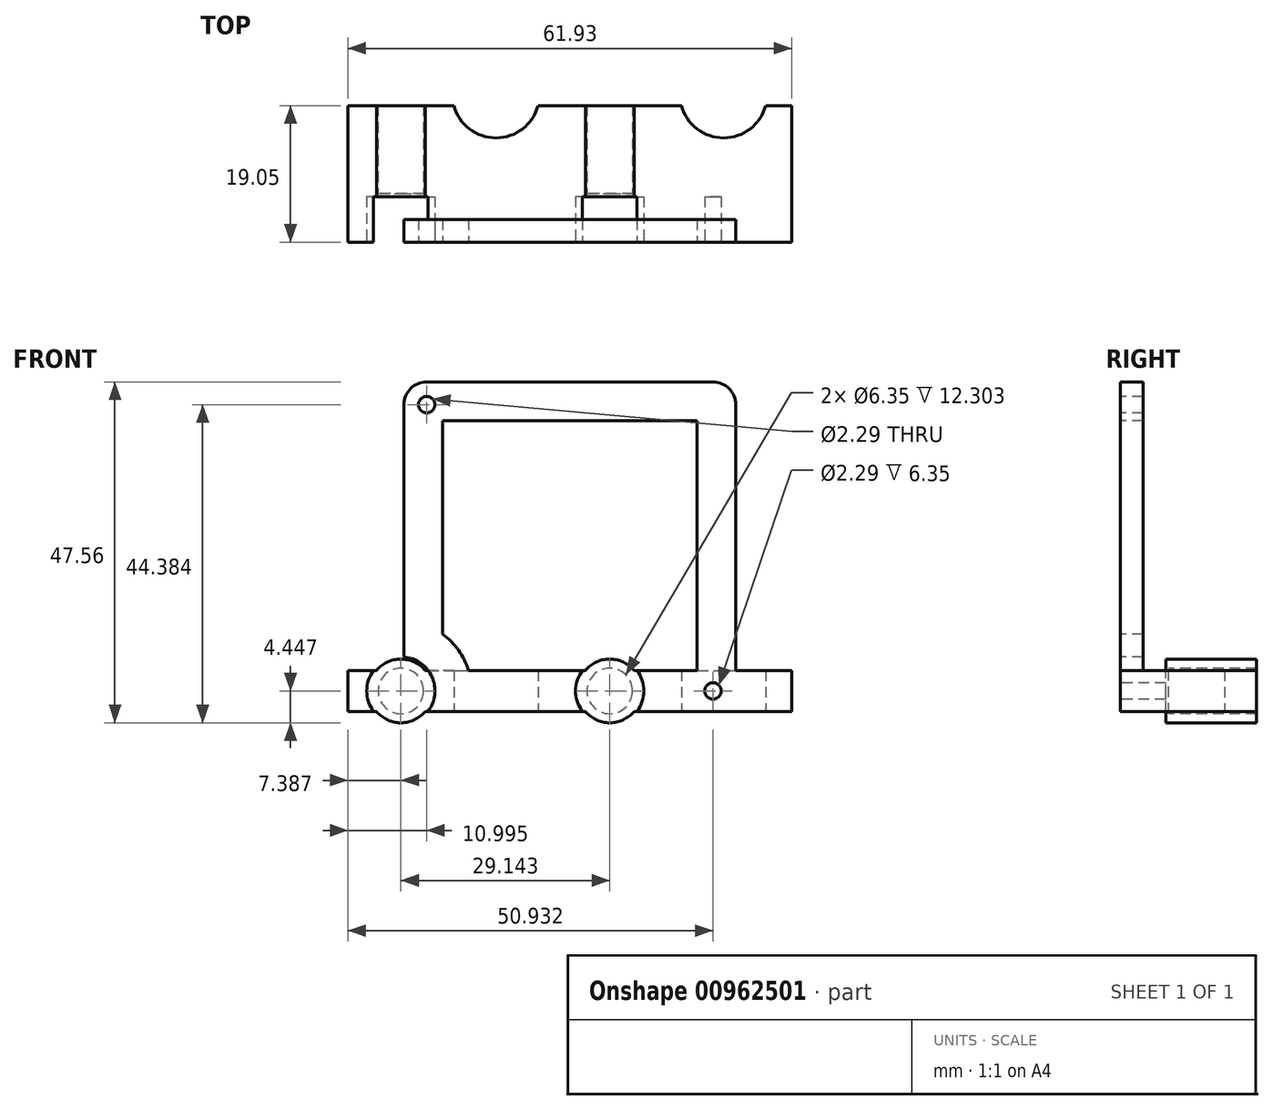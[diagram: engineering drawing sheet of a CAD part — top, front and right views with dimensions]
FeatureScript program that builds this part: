
annotation { "Feature Type Name" : "Feature", "Feature Type Description" : "" }
export const myFeature = defineFeature(function(context is Context, id is Id, definition is map)
    precondition{}
    {
        {
            var Q0;
            Q0=qCreatedBy(makeId("Top.planeOp"),FACE);
            var sketch = newSketch(context, id + "F0", { "sketchPlane" : qUnion([Q0])});
            skArc(sketch, "E0", {"start": v(-21.76, -1.59) * mm, "mid": v(-15.88, -6.1) * mm, "end": v(-9.99, -1.59) * mm});
            skArc(sketch, "E1", {"start": v(9.99, -1.59) * mm, "mid": v(15.88, -6.1) * mm, "end": v(21.76, -1.59) * mm});
            skLineSegment(sketch, "E2", {"start": v(-21.76, -1.59) * mm, "end": v(-36.53, -1.59) * mm});
            skLineSegment(sketch, "E3", {"start": v(-36.53, -1.59) * mm, "end": v(-36.53, -20.64) * mm});
            skLineSegment(sketch, "E4", {"start": v(-36.53, -20.64) * mm, "end": v(25.4, -20.64) * mm});
            skLineSegment(sketch, "E5", {"start": v(25.4, -20.64) * mm, "end": v(25.4, -1.59) * mm});
            skLineSegment(sketch, "E6", {"start": v(25.4, -1.59) * mm, "end": v(21.76, -1.59) * mm});
            skLineSegment(sketch, "E7", {"start": v(9.99, -1.59) * mm, "end": v(-9.99, -1.59) * mm});
            skSolve(sketch);
        }
        {
            var Q0;
            Q0 = qSketchRegion(id + "F0", true);
            extrude(context, id + "F1", {"entities" : qUnion([Q0]), "depth" : 5.7 * mm, "offsetDistance" : 25.4 * mm});
        }
        {
            var Q0;
            Q0=makeQuery(id+"F1.opExtrude","SWEPT_FACE",FACE,{"disambiguationData":[OSD([sQuery(id+"F0.wireOp",EDGE,"E4")])]});
            var sketch = newSketch(context, id + "F2", { "sketchPlane" : qUnion([Q0])});
            skCircle(sketch, "E8", {"center": v(-5.56, 2.86) * mm, "radius": 2.86 * mm, "construction": true});
            skCircle(sketch, "E9", {"center": v(-25.53, 42.8) * mm, "radius": 1.14 * mm});
            skLineSegment(sketch, "E10", {"start": v(-28.7, 42.8) * mm, "end": v(-28.7, 5.71) * mm});
            skLineSegment(sketch, "E11", {"start": v(-28.7, 5.71) * mm, "end": v(-23.29, 5.72) * mm});
            skLineSegment(sketch, "E12", {"start": v(-23.29, 5.72) * mm, "end": v(-23.29, 40.55) * mm});
            skPoint(sketch, "E13.top.start.orphan", {"position": v(-29.18, -20.76) * mm});
            skCircle(sketch, "E14", {"center": v(14.4, 2.86) * mm, "radius": 1.14 * mm});
            skLineSegment(sketch, "E15", {"start": v(-25.53, 42.8) * mm, "end": v(14.4, 2.86) * mm, "construction": true});
            skArc(sketch, "E16", {"start": v(17.58, 42.8) * mm, "mid": v(16.65, 45.04) * mm, "end": v(14.4, 45.97) * mm});
            skLineSegment(sketch, "E17", {"start": v(17.58, 42.8) * mm, "end": v(17.58, 5.72) * mm});
            skLineSegment(sketch, "E18", {"start": v(12.16, 5.72) * mm, "end": v(17.58, 5.71) * mm});
            skLineSegment(sketch, "E19", {"start": v(-25.53, 45.97) * mm, "end": v(14.4, 45.97) * mm});
            skArc(sketch, "E20", {"start": v(-25.53, 45.97) * mm, "mid": v(-27.78, 45.04) * mm, "end": v(-28.7, 42.8) * mm});
            skLineSegment(sketch, "E21", {"start": v(-23.29, 40.55) * mm, "end": v(12.16, 40.55) * mm});
            skLineSegment(sketch, "E22", {"start": v(12.16, 40.55) * mm, "end": v(12.16, 5.72) * mm});
            skSolve(sketch);
        }
        {
            var Q0;
            Q0 = qSketchRegion(id + "F2", true);
            extrude(context, id + "F3", {"entities" : qUnion([Q0]), "operationType" : NewBodyOperationType.ADD, "oppositeDirection" : true, "depth" : 3.17 * mm, "offsetDistance" : 25.4 * mm});
        }
        {
            var Q0;
            Q0=makeQuery(id+"F3.boolean.opBoolean","MERGE",FACE,{"derivedFrom":[makeQuery(id+"F1.opExtrude","SWEPT_FACE",FACE,{"disambiguationData":[OSD([sQuery(id+"F0.wireOp",EDGE,"E4")])]}),makeQuery(id+"F3.opExtrude","CAP_FACE",FACE,{"disambiguationData":[OSD([sQuery(id+"F2.wireOp",EDGE,"E9"),sQuery(id+"F2.wireOp",EDGE,"GDH4g0oQ-nd7Q-Zn2g-Z2z6-5aHBvg0Lr09C"),sQuery(id+"F2.wireOp",EDGE,"E10"),sQuery(id+"F2.wireOp",EDGE,"E11"),sQuery(id+"F2.wireOp",EDGE,"E12")])],"isStart":true}),makeQuery(id+"F3.opExtrude","CAP_FACE",FACE,{"disambiguationData":[OSD([sQuery(id+"F2.wireOp",EDGE,"nM6Eh8F1-qOBL-3qUv-6L2V-JEi5WRzBgLFH"),sQuery(id+"F2.wireOp",EDGE,"JC2lydbS-xeSN-gWn7-KMeQ-zuUTK9r0PLlo"),sQuery(id+"F2.wireOp",EDGE,"ONUtfR4M-aSmu-eGrm-hsvk-2R0VDrcKPRzi"),sQuery(id+"F2.wireOp",EDGE,"0aukuiJN-D17R-zCOD-Oj78-UeWdiGfD59D5"),sQuery(id+"F2.wireOp",EDGE,"T4R5p8lt-zdvz-CFuB-Jltc-x5WoAOuWlztu")])],"isStart":true})]});
            var sketch = newSketch(context, id + "F4", { "sketchPlane" : qUnion([Q0])});
            skCircle(sketch, "E23", {"center": v(-29.14, 2.86) * mm, "radius": 3.18 * mm});
            skCircle(sketch, "E24", {"center": v(0, 2.86) * mm, "radius": 3.18 * mm});
            skLineSegment(sketch, "E25", {"start": v(-36.53, 2.86) * mm, "end": v(-21.76, 2.86) * mm, "construction": true});
            skLineSegment(sketch, "E26", {"start": v(-9.99, 2.86) * mm, "end": v(9.99, 2.86) * mm, "construction": true});
            skSolve(sketch);
        }
        {
            var Q0;
            {var subQ0=sQuery(id+"F2.wireOp",EDGE,"E20");var subQ1=sQuery(id+"F2.wireOp",EDGE,"E19");var subQ2=sQuery(id+"F2.wireOp",EDGE,"E16");var subQ3=sQuery(id+"F2.wireOp",EDGE,"E10");var subQ4=sQuery(id+"F2.wireOp",EDGE,"E17");var subQ7=sQuery(id+"F0.wireOp",EDGE,"E5");var subQ8=sQuery(id+"F0.wireOp",EDGE,"E4");var subQ13=sQuery(id+"F2.wireOp",EDGE,"E9");var subQ14=sQuery(id+"F2.wireOp",EDGE,"E12");var subQ15=sQuery(id+"F2.wireOp",EDGE,"E21");var subQ16=sQuery(id+"F2.wireOp",EDGE,"E22");Q0=makeQuery(id+"F9.boolean.opBoolean","SPLIT",FACE,{"disambiguationData":[TD([makeQuery(id+"F1.opExtrude","SWEPT_FACE",FACE,{"disambiguationData":[OSD([subQ7])]})])],"derivedFrom":makeQuery(id+"F3.boolean.opBoolean","MERGE",FACE,{"derivedFrom":[makeQuery(id+"F1.opExtrude","SWEPT_FACE",FACE,{"disambiguationData":[OSD([subQ8])]}),makeQuery(id+"F3.opExtrude","CAP_FACE",FACE,{"disambiguationData":[OSD([subQ13,subQ3,sQuery(id+"F2.wireOp",EDGE,"E11"),subQ14,subQ2,subQ4,sQuery(id+"F2.wireOp",EDGE,"E18"),subQ1,subQ0,subQ15,subQ16])],"isStart":true})]})});}
            var sketch = newSketch(context, id + "F5", { "sketchPlane" : qUnion([Q0])});
            skCircle(sketch, "E27", {"center": v(-29.14, 2.86) * mm, "radius": 4.45 * mm});
            skCircle(sketch, "E28", {"center": v(0, 2.86) * mm, "radius": 4.45 * mm});
            skSolve(sketch);
        }
        {
            var Q0;
            Q0 = qSketchRegion(id + "F5", true);
            var Q1;
            Q1=makeQuery(id+"F1.opExtrude","SWEPT_FACE",FACE,{"disambiguationData":[OSD([sQuery(id+"F0.wireOp",EDGE,"E2")])]});
            extrude(context, id + "F6", {"entities" : qUnion([Q0]), "operationType" : NewBodyOperationType.ADD, "endBound" : BoundingType.UP_TO_SURFACE, "oppositeDirection" : true, "depth" : 25.4 * mm, "endBoundEntityFace" : qUnion([Q1]), "offsetDistance" : 25.4 * mm});
        }
        {
            var Q0;
            Q0 = qSketchRegion(id + "F4", true);
            extrude(context, id + "F7", {"entities" : qUnion([Q0]), "operationType" : NewBodyOperationType.REMOVE, "endBound" : BoundingType.UP_TO_NEXT, "oppositeDirection" : true, "depth" : 23.37 * mm, "offsetDistance" : 25.4 * mm});
        }
        {
            var Q0;
            Q0=makeQuery(id+"F3.boolean.opBoolean","MERGE",FACE,{"derivedFrom":[makeQuery(id+"F1.opExtrude","SWEPT_FACE",FACE,{"disambiguationData":[OSD([sQuery(id+"F0.wireOp",EDGE,"E4")])]}),makeQuery(id+"F3.opExtrude","CAP_FACE",FACE,{"disambiguationData":[OSD([sQuery(id+"F2.wireOp",EDGE,"E9"),sQuery(id+"F2.wireOp",EDGE,"GDH4g0oQ-nd7Q-Zn2g-Z2z6-5aHBvg0Lr09C"),sQuery(id+"F2.wireOp",EDGE,"E10"),sQuery(id+"F2.wireOp",EDGE,"E11"),sQuery(id+"F2.wireOp",EDGE,"E12")])],"isStart":true}),makeQuery(id+"F3.opExtrude","CAP_FACE",FACE,{"disambiguationData":[OSD([sQuery(id+"F2.wireOp",EDGE,"nM6Eh8F1-qOBL-3qUv-6L2V-JEi5WRzBgLFH"),sQuery(id+"F2.wireOp",EDGE,"JC2lydbS-xeSN-gWn7-KMeQ-zuUTK9r0PLlo"),sQuery(id+"F2.wireOp",EDGE,"ONUtfR4M-aSmu-eGrm-hsvk-2R0VDrcKPRzi"),sQuery(id+"F2.wireOp",EDGE,"0aukuiJN-D17R-zCOD-Oj78-UeWdiGfD59D5"),sQuery(id+"F2.wireOp",EDGE,"T4R5p8lt-zdvz-CFuB-Jltc-x5WoAOuWlztu")])],"isStart":true})]});
            var sketch = newSketch(context, id + "F8", { "sketchPlane" : qUnion([Q0])});
            skCircle(sketch, "E29", {"center": v(-29.14, 2.86) * mm, "radius": 4.76 * mm});
            skCircle(sketch, "E30", {"center": v(0, 2.86) * mm, "radius": 4.76 * mm});
            skSolve(sketch);
        }
        {
            var Q0;
            Q0 = qSketchRegion(id + "F8", true);
            extrude(context, id + "F9", {"entities" : qUnion([Q0]), "operationType" : NewBodyOperationType.REMOVE, "oppositeDirection" : true, "depth" : 6.35 * mm, "offsetDistance" : 25.4 * mm});
        }
        {
            var Q0;
            {var subQ0=sQuery(id+"F2.wireOp",EDGE,"E20");var subQ1=sQuery(id+"F2.wireOp",EDGE,"E19");var subQ2=sQuery(id+"F2.wireOp",EDGE,"E16");var subQ3=sQuery(id+"F2.wireOp",EDGE,"E10");var subQ4=sQuery(id+"F2.wireOp",EDGE,"E17");var subQ7=sQuery(id+"F0.wireOp",EDGE,"E5");var subQ8=sQuery(id+"F0.wireOp",EDGE,"E4");var subQ13=sQuery(id+"F2.wireOp",EDGE,"E9");var subQ14=sQuery(id+"F2.wireOp",EDGE,"E12");var subQ15=sQuery(id+"F2.wireOp",EDGE,"E21");var subQ16=sQuery(id+"F2.wireOp",EDGE,"E22");Q0=makeQuery(id+"F9.boolean.opBoolean","SPLIT",FACE,{"disambiguationData":[TD([makeQuery(id+"F1.opExtrude","SWEPT_FACE",FACE,{"disambiguationData":[OSD([subQ7])]})])],"derivedFrom":makeQuery(id+"F3.boolean.opBoolean","MERGE",FACE,{"derivedFrom":[makeQuery(id+"F1.opExtrude","SWEPT_FACE",FACE,{"disambiguationData":[OSD([subQ8])]}),makeQuery(id+"F3.opExtrude","CAP_FACE",FACE,{"disambiguationData":[OSD([subQ13,subQ3,sQuery(id+"F2.wireOp",EDGE,"E11"),subQ14,subQ2,subQ4,sQuery(id+"F2.wireOp",EDGE,"E18"),subQ1,subQ0,subQ15,subQ16])],"isStart":true})]})});}
            var sketch = newSketch(context, id + "F10", { "sketchPlane" : qUnion([Q0])});
            skCircle(sketch, "E31", {"center": v(14.4, 2.86) * mm, "radius": 1.14 * mm});
            skSolve(sketch);
        }
        {
            var Q0;
            Q0 = qSketchRegion(id + "F10", true);
            extrude(context, id + "F11", {"entities" : qUnion([Q0]), "operationType" : NewBodyOperationType.REMOVE, "oppositeDirection" : true, "depth" : 6.35 * mm, "offsetDistance" : 25.4 * mm});
        }
        {
            var Q0;
            {var subQ0=sQuery(id+"F2.wireOp",EDGE,"E20");var subQ1=sQuery(id+"F2.wireOp",EDGE,"E19");var subQ2=sQuery(id+"F2.wireOp",EDGE,"E16");var subQ3=sQuery(id+"F2.wireOp",EDGE,"E10");var subQ4=sQuery(id+"F2.wireOp",EDGE,"E17");var subQ7=sQuery(id+"F0.wireOp",EDGE,"E5");var subQ8=sQuery(id+"F0.wireOp",EDGE,"E4");var subQ13=sQuery(id+"F2.wireOp",EDGE,"E9");var subQ14=sQuery(id+"F2.wireOp",EDGE,"E12");var subQ15=sQuery(id+"F2.wireOp",EDGE,"E21");var subQ16=sQuery(id+"F2.wireOp",EDGE,"E22");Q0=makeQuery(id+"F9.boolean.opBoolean","SPLIT",FACE,{"disambiguationData":[TD([makeQuery(id+"F1.opExtrude","SWEPT_FACE",FACE,{"disambiguationData":[OSD([subQ7])]})])],"derivedFrom":makeQuery(id+"F6.boolean.opBoolean","MERGE",FACE,{"derivedFrom":[makeQuery(id+"F3.boolean.opBoolean","MERGE",FACE,{"derivedFrom":[makeQuery(id+"F1.opExtrude","SWEPT_FACE",FACE,{"disambiguationData":[OSD([subQ8])]}),makeQuery(id+"F3.opExtrude","CAP_FACE",FACE,{"disambiguationData":[OSD([subQ13,subQ3,sQuery(id+"F2.wireOp",EDGE,"E11"),subQ14,subQ2,subQ4,sQuery(id+"F2.wireOp",EDGE,"E18"),subQ1,subQ0,subQ15,subQ16])],"isStart":true})]}),makeQuery(id+"F6.opExtrude","CAP_FACE",FACE,{"disambiguationData":[OSD([sQuery(id+"F5.wireOp",EDGE,"E27")])],"isStart":true}),makeQuery(id+"F6.opExtrude","CAP_FACE",FACE,{"disambiguationData":[OSD([sQuery(id+"F5.wireOp",EDGE,"E28")])],"isStart":true})]})});}
            var sketch = newSketch(context, id + "F12", { "sketchPlane" : qUnion([Q0])});
            skArc(sketch, "E32", {"start": v(-19.72, 0) * mm, "mid": v(-21.11, 8.55) * mm, "end": v(-28.7, 12.7) * mm});
            skArc(sketch, "E33", {"start": v(-25.33, 0) * mm, "mid": v(-24.8, 4.8) * mm, "end": v(-28.7, 7.6) * mm});
            skLineSegment(sketch, "E34", {"start": v(-28.7, 12.7) * mm, "end": v(-28.7, 7.6) * mm});
            skLineSegment(sketch, "E35", {"start": v(-25.33, 0) * mm, "end": v(-19.72, 0) * mm});
            skSolve(sketch);
        }
        {
            var Q0;
            Q0 = qSketchRegion(id + "F12", true);
            var Q1;
            Q1=makeQuery(id+"F3.opExtrude","CAP_FACE",FACE,{"disambiguationData":[OSD([sQuery(id+"F2.wireOp",EDGE,"E9"),sQuery(id+"F2.wireOp",EDGE,"E10"),sQuery(id+"F2.wireOp",EDGE,"E11"),sQuery(id+"F2.wireOp",EDGE,"E12"),sQuery(id+"F2.wireOp",EDGE,"E16"),sQuery(id+"F2.wireOp",EDGE,"E17"),sQuery(id+"F2.wireOp",EDGE,"E18"),sQuery(id+"F2.wireOp",EDGE,"E19"),sQuery(id+"F2.wireOp",EDGE,"E20"),sQuery(id+"F2.wireOp",EDGE,"E21"),sQuery(id+"F2.wireOp",EDGE,"E22")])],"isStart":false});
            extrude(context, id + "F13", {"entities" : qUnion([Q0]), "operationType" : NewBodyOperationType.ADD, "endBound" : BoundingType.UP_TO_SURFACE, "oppositeDirection" : true, "depth" : 25.4 * mm, "endBoundEntityFace" : qUnion([Q1]), "offsetDistance" : 25.4 * mm});
        }
        {
            var Q0;
            Q0=makeQuery(id+"F9.boolean.opBoolean","COPY",FACE,{"derivedFrom":makeQuery(id+"F9.opExtrude","CAP_FACE",FACE,{"disambiguationData":[OSD([sQuery(id+"F8.wireOp",EDGE,"E30")])],"isStart":false})});
            var sketch = newSketch(context, id + "F14", { "sketchPlane" : qUnion([Q0])});
            skCircle(sketch, "E36", {"center": v(0, 2.86) * mm, "radius": 3.18 * mm});
            skCircle(sketch, "E37", {"center": v(-29.14, 2.86) * mm, "radius": 3.18 * mm});
            skSolve(sketch);
        }
        {
            var Q0;
            Q0 = qSketchRegion(id + "F14", true);
            extrude(context, id + "F15", {"entities" : qUnion([Q0]), "operationType" : NewBodyOperationType.ADD, "oppositeDirection" : true, "depth" : 0.4 * mm, "offsetDistance" : 25.4 * mm});
        }
    });
